# Revit family: 24-RHLI-90
name_source: partatom
category: Plumbing Fixtures
units: mm (PartAtom-declared; Revit-internal decimal feet)

## family parameters
Always vertical = Yes
Cut with Voids When Loaded = No
OmniClass Number = 23.45.00.00
OmniClass Title = Sanitary, Laundry, and Cleaning Equipment
Part Type = Normal
Room Calculation Point = No
Round Connector Dimension = Use Diameter
Shared = No
Work Plane-Based = No

## types (2) — shared parameters
Brass Chromed = Brass
Cast Iron Cover = Iron, Cast
Default Elevation = 0.000"
Installation Thread = 2" - 11 ½ NPSM; Use A Ceramic Insert Of 10,6 x 2,36 x 0,39"
Manufacturer = HELVEX
Materials = Against Chrome Finish; Base Cylindrical Gray Cast Iron ASTM A 48 Class 25
To Dislodge Volume of Flow = 9.2 gal/min
Type Comments = Drains

## per-type parameters (varying)
| type | Accessories | Data Sheet | Description | Features | Type Image | URL |
| 24-RHLI | Hydraulic Seal 0,052 gal; Includes Setting Maintenance Tool | http://helvex.com | Strainer with Contour Drain for Ceramic Insert | Rectangular Strainer A Mouth; With Drainage Contour; 0,75" Installation Adjustment | <None> | http://helvex.com |
| 24-RHLI-90 |  | https://www.helvex.com.mx | Coladera rectangular alargada 90cm | Coladera rectangular alargada 90cm | 24-RHLI-90.jpg | https://www.helvex.com.mx |

note: column(s) folded — value = type name in every type: Model

## geometry (parser evidence)
native form markers: Sweep x3
no freeform markers — native parametric forms only
